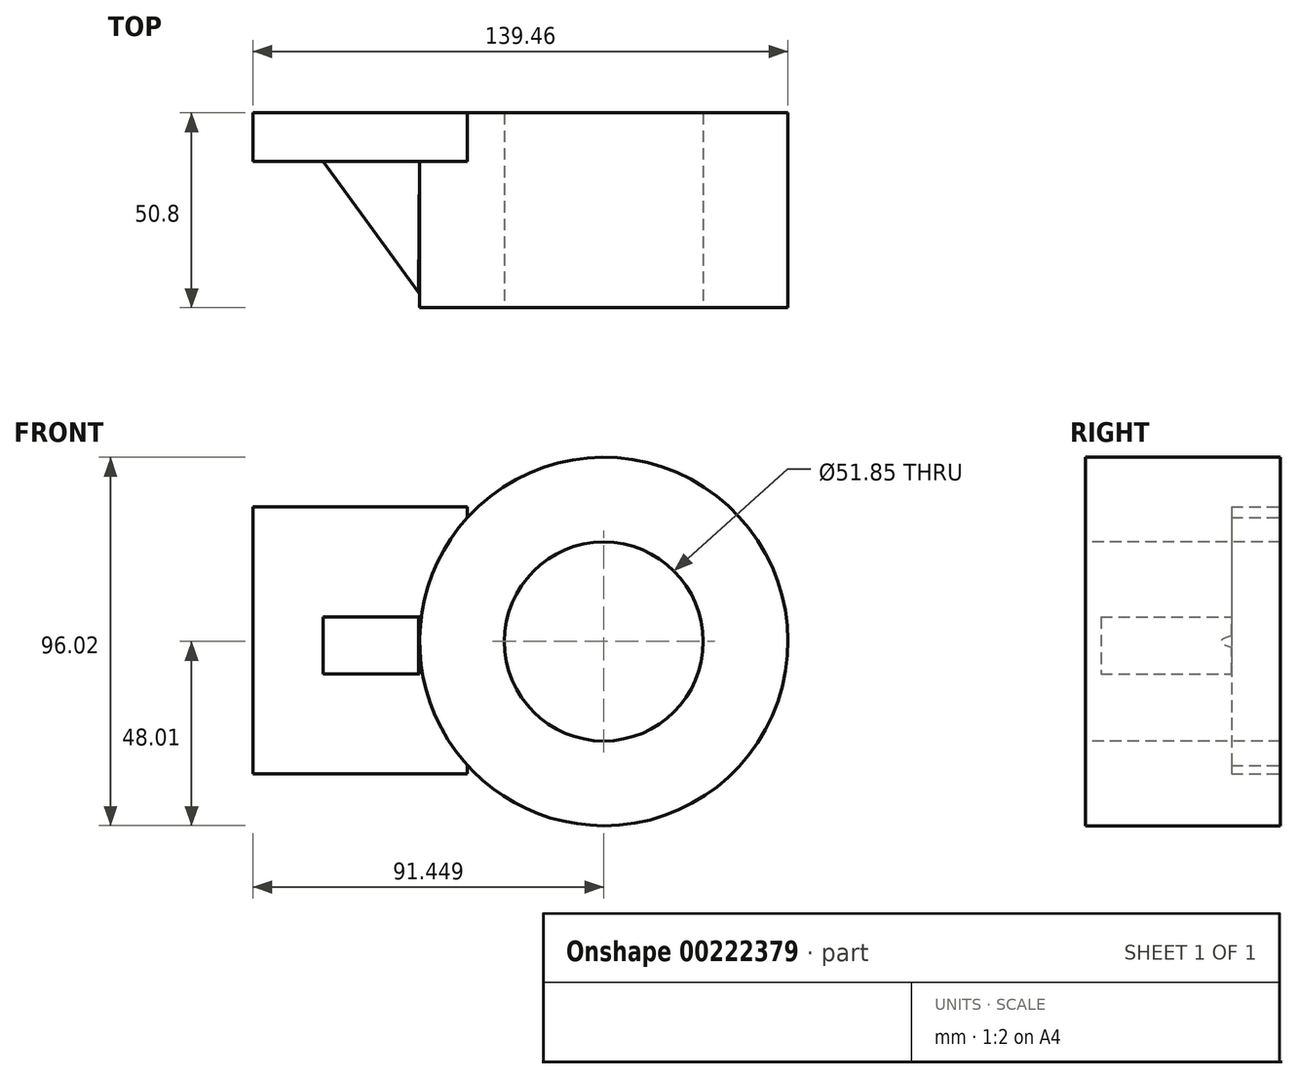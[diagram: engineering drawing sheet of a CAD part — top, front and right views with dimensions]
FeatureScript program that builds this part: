
annotation { "Feature Type Name" : "Feature", "Feature Type Description" : "" }
export const myFeature = defineFeature(function(context is Context, id is Id, definition is map)
    precondition{}
    {
        {
            var Q0;
            Q0=qCreatedBy(makeId("Front.planeOp"),FACE);
            var sketch = newSketch(context, id + "F0", { "sketchPlane" : qUnion([Q0])});
            skLineSegment(sketch, "E0.bottom", {"start": v(0, 35.16) * mm, "end": v(-55.92, 35.16) * mm});
            skLineSegment(sketch, "E0.top", {"start": v(0, -34.45) * mm, "end": v(-55.92, -34.45) * mm});
            skLineSegment(sketch, "E0.left", {"start": v(0, 35.16) * mm, "end": v(0, -34.45) * mm});
            skLineSegment(sketch, "E0.right", {"start": v(-55.92, 35.16) * mm, "end": v(-55.92, -34.45) * mm});
            skSolve(sketch);
        }
        {
            var Q0;
            Q0=qCreatedBy(makeId("Front.planeOp"),FACE);
            var sketch = newSketch(context, id + "F1", { "sketchPlane" : qUnion([Q0])});
            skCircle(sketch, "E1", {"center": v(35.53, 0) * mm, "radius": 48.01 * mm});
            skSolve(sketch);
        }
        {
            var Q0;
            Q0=makeQuery(id+"F1.imprint","IMPRINT",FACE,{"disambiguationData":[TD([[makeQuery(id+"F1.imprint","IMPRINT",EDGE,{"derivedFrom":sQuery(id+"F1.wireOp",EDGE,"E1")}),1.0]])]});
            extrude(context, id + "F2", {"entities" : qUnion([Q0]), "depth" : 50.8 * mm});
        }
        {
            var Q0;
            Q0=makeQuery(id+"F0.imprint","IMPRINT",FACE,{"disambiguationData":[TD([[makeQuery(id+"F0.imprint","IMPRINT",EDGE,{"derivedFrom":sQuery(id+"F0.wireOp",EDGE,"E0.bottom")}),1.0]])]});
            extrude(context, id + "F5", {"entities" : qUnion([Q0]), "operationType" : NewBodyOperationType.ADD, "depth" : 12.7 * mm});
        }
        {
            var Q0;
            Q0=makeQuery(id+"F2.opExtrude","CAP_FACE",FACE,{"disambiguationData":[OSD([sQuery(id+"F1.wireOp",EDGE,"E1")])],"isStart":false});
            var sketch = newSketch(context, id + "F6", { "sketchPlane" : qUnion([Q0])});
            skCircle(sketch, "E2", {"center": v(35.53, 0) * mm, "radius": 25.93 * mm});
            skSolve(sketch);
        }
        {
            var Q0;
            Q0=makeQuery(id+"F6.imprint","IMPRINT",FACE,{"disambiguationData":[TD([[makeQuery(id+"F6.imprint","IMPRINT",EDGE,{"derivedFrom":sQuery(id+"F6.wireOp",EDGE,"E2")}),1.0]])]});
            extrude(context, id + "F3", {"entities" : qUnion([Q0]), "operationType" : NewBodyOperationType.REMOVE, "endBound" : BoundingType.THROUGH_ALL, "oppositeDirection" : true, "depth" : 25.4 * mm});
        }
        {
            var Q0;
            Q0=qCreatedBy(makeId("Top.planeOp"),FACE);
            var sketch = newSketch(context, id + "F7", { "sketchPlane" : qUnion([Q0])});
            skLineSegment(sketch, "E3", {"start": v(-12.74, -46.77) * mm, "end": v(-37.66, -12.62) * mm});
            skLineSegment(sketch, "E4", {"start": v(-37.66, -12.62) * mm, "end": v(-12.46, -12.37) * mm});
            skLineSegment(sketch, "E5", {"start": v(-12.46, -12.37) * mm, "end": v(-12.74, -46.77) * mm});
            skSolve(sketch);
        }
        {
            var Q0;
            Q0=makeQuery(id+"F7.imprint","IMPRINT",FACE,{"disambiguationData":[TD([[makeQuery(id+"F7.imprint","IMPRINT",EDGE,{"derivedFrom":sQuery(id+"F7.wireOp",EDGE,"E3")}),-1.0]])]});
            extrude(context, id + "F4", {"entities" : qUnion([Q0]), "operationType" : NewBodyOperationType.ADD, "depth" : 6.35 * mm, "hasSecondDirection" : true, "secondDirectionOppositeDirection" : true, "secondDirectionDepth" : 8.47 * mm});
        }
    });
